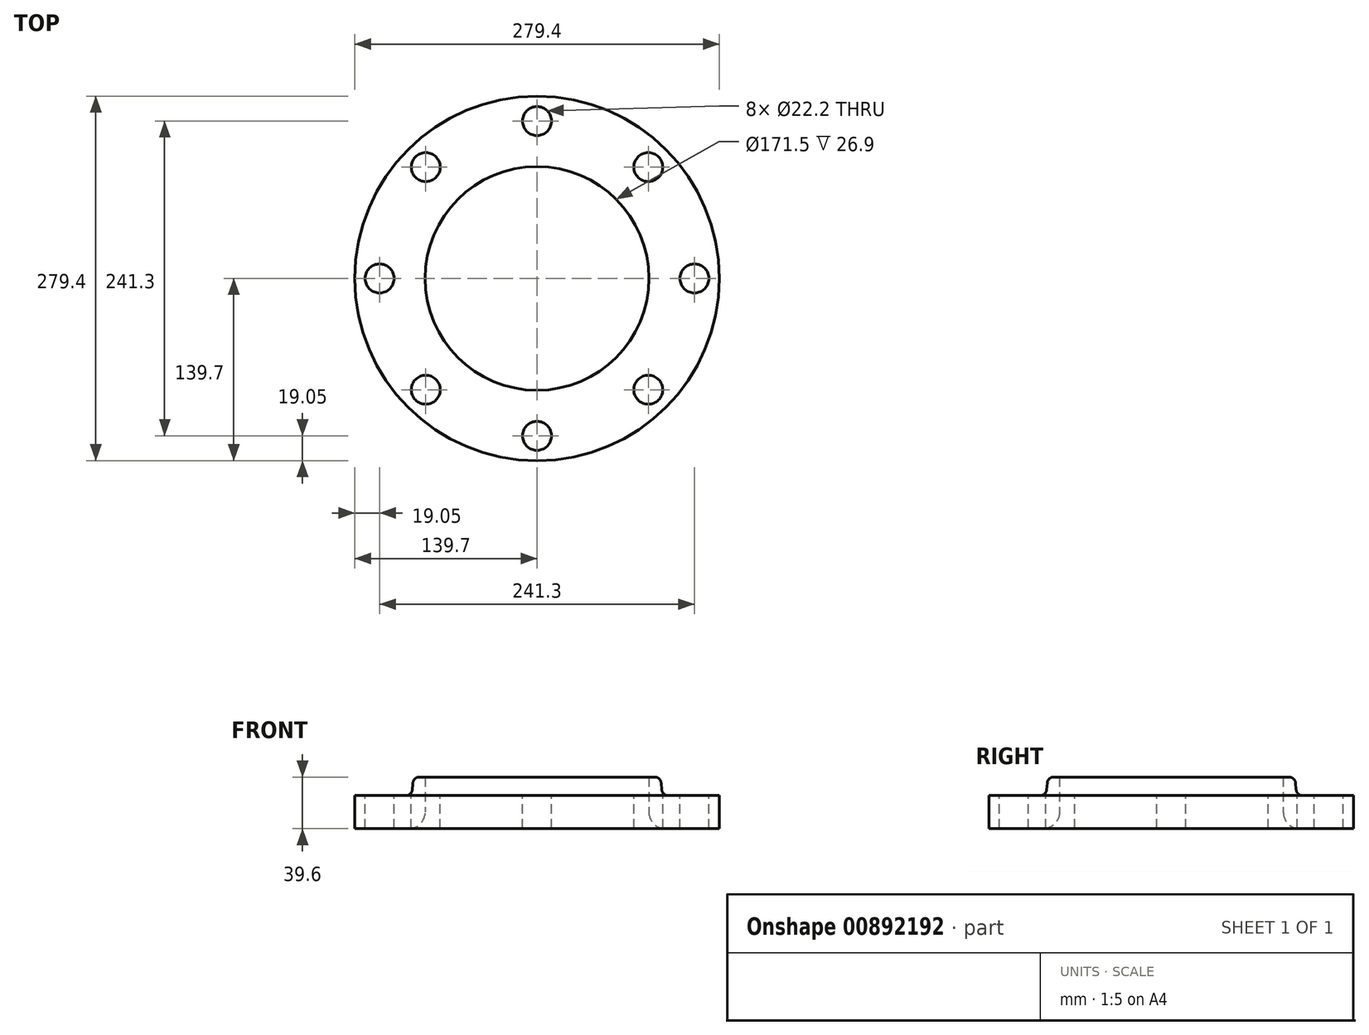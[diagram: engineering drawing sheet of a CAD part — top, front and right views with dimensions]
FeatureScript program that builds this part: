
annotation { "Feature Type Name" : "Feature", "Feature Type Description" : "" }
export const myFeature = defineFeature(function(context is Context, id is Id, definition is map)
    precondition{}
    {
        {
            var Q0;
            Q0=qCreatedBy(makeId("Front.planeOp"),FACE);
            var sketch = newSketch(context, id + "F0", { "sketchPlane" : qUnion([Q0])});
            skLineSegment(sketch, "E0", {"start": v(98.45, 0) * mm, "end": v(139.7, 0) * mm});
            skLineSegment(sketch, "E1", {"start": v(139.7, 0) * mm, "end": v(139.7, 25.4) * mm});
            skLineSegment(sketch, "E2", {"start": v(139.7, 25.4) * mm, "end": v(100.58, 25.4) * mm});
            skLineSegment(sketch, "E3", {"start": v(95.6, 29.96) * mm, "end": v(95.16, 35.04) * mm});
            skLineSegment(sketch, "E4", {"start": v(90.18, 39.6) * mm, "end": v(85.75, 39.6) * mm});
            skLineSegment(sketch, "E5", {"start": v(85.75, 39.6) * mm, "end": v(85.75, 12.7) * mm});
            skLineSegment(sketch, "E6", {"start": v(0, 0) * mm, "end": v(0, 39.6) * mm});
            skPoint(sketch, "E7.visualSharp", {"position": v(94.76, 39.6) * mm});
            skArc(sketch, "E7.filletArc", {"start": v(95.16, 35.04) * mm, "mid": v(93.55, 38.29) * mm, "end": v(90.18, 39.6) * mm});
            skPoint(sketch, "E8.visualSharp", {"position": v(96, 25.4) * mm});
            skArc(sketch, "E8.filletArc", {"start": v(95.6, 29.96) * mm, "mid": v(97.2, 26.71) * mm, "end": v(100.58, 25.4) * mm});
            skPoint(sketch, "E9.visualSharp", {"position": v(85.75, 0) * mm});
            skArc(sketch, "E9.filletArc", {"start": v(85.75, 12.7) * mm, "mid": v(89.47, 3.72) * mm, "end": v(98.45, 0) * mm});
            skSolve(sketch);
        }
        {
            var Q0;
            Q0=makeQuery(id+"F0.imprint","IMPRINT",FACE,{"disambiguationData":[TD([[makeQuery(id+"F0.imprint","IMPRINT",EDGE,{"derivedFrom":sQuery(id+"F0.wireOp",EDGE,"newPmkzC-CrfG-sXBi-HGfB-OUHVhpxAI036")}),1.0]])]});
            var Q1;
            Q1=makeQuery(id+"F0.imprint","IMPRINT",FACE,{"disambiguationData":[TD([[makeQuery(id+"F0.imprint","IMPRINT",EDGE,{"derivedFrom":sQuery(id+"F0.wireOp",EDGE,"E0")}),1.0]])]});
            var Q2;
            Q2=sQuery(id+"F0.wireOp",EDGE,"E6");
            revolve(context, id + "F1", {"surfaceOperationType" : NewSurfaceOperationType.NEW, "entities" : qUnion([Q0, Q1]), "axis" : qUnion([Q2]), "revolveType" : RevolveType.FULL});
        }
        {
            var Q0;
            Q0=makeQuery(id+"F1.opRevolve","SWEPT_FACE",FACE,{"disambiguationData":[OSD([sQuery(id+"F0.wireOp",EDGE,"E2")])]});
            var sketch = newSketch(context, id + "F2", { "sketchPlane" : qUnion([Q0])});
            skCircle(sketch, "E10", {"center": v(0, 0) * mm, "radius": 120.65 * mm, "construction": true});
            skCircle(sketch, "E11", {"center": v(0, 120.65) * mm, "radius": 11.1 * mm});
            skCircle(sketch, "E12.1.0", {"center": v(-85.31, 85.31) * mm, "radius": 11.1 * mm});
            skCircle(sketch, "E12.2.0", {"center": v(-120.65, 0) * mm, "radius": 11.1 * mm});
            skCircle(sketch, "E12.3.0", {"center": v(-85.31, -85.31) * mm, "radius": 11.1 * mm});
            skCircle(sketch, "E12.4.0", {"center": v(0, -120.65) * mm, "radius": 11.1 * mm});
            skCircle(sketch, "E12.5.0", {"center": v(85.31, -85.31) * mm, "radius": 11.1 * mm});
            skCircle(sketch, "E12.6.0", {"center": v(120.65, 0) * mm, "radius": 11.1 * mm});
            skCircle(sketch, "E12.7.0", {"center": v(85.31, 85.31) * mm, "radius": 11.1 * mm});
            skSolve(sketch);
        }
        {
            var Q0;
            Q0=qSketchRegion(id+"F2",true);
            extrude(context, id + "F3", {"entities" : qUnion([Q0]), "operationType" : NewBodyOperationType.REMOVE, "endBound" : BoundingType.THROUGH_ALL, "oppositeDirection" : true, "depth" : 25 * mm, "offsetDistance" : 25 * mm});
        }
    });
